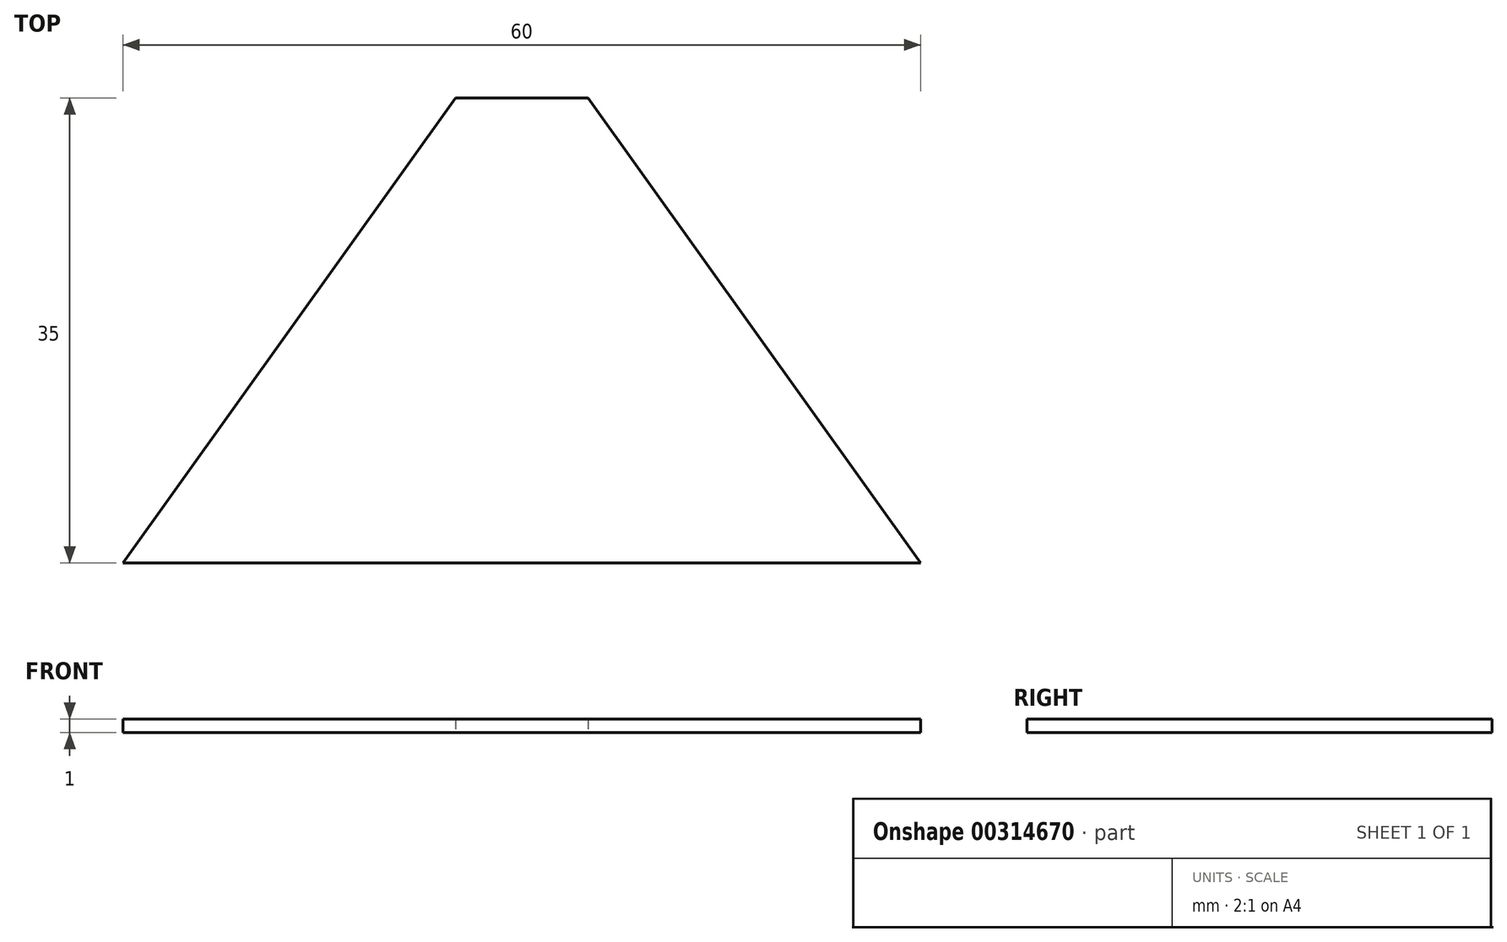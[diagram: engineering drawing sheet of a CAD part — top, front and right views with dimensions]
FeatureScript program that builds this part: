
annotation { "Feature Type Name" : "Feature", "Feature Type Description" : "" }
export const myFeature = defineFeature(function(context is Context, id is Id, definition is map)
    precondition{}
    {
        {
            var Q0;
            Q0=qCreatedBy(makeId("Top.planeOp"),FACE);
            var sketch = newSketch(context, id + "F0", { "sketchPlane" : qUnion([Q0])});
            skLineSegment(sketch, "E0", {"start": v(0, 0) * mm, "end": v(0, 35) * mm, "construction": true});
            skLineSegment(sketch, "E1", {"start": v(0, 0) * mm, "end": v(-30, 0) * mm});
            skLineSegment(sketch, "E2", {"start": v(0, 35) * mm, "end": v(-5, 35) * mm});
            skLineSegment(sketch, "E3", {"start": v(-5, 35) * mm, "end": v(-30, 0) * mm});
            skLineSegment(sketch, "E4.MirrorCS", {"start": v(0, 35) * mm, "end": v(5, 35) * mm});
            skLineSegment(sketch, "E5.MirrorCS", {"start": v(5, 35) * mm, "end": v(30, 0) * mm});
            skLineSegment(sketch, "E6.MirrorCS", {"start": v(0, 0) * mm, "end": v(30, 0) * mm});
            skSolve(sketch);
        }
        {
            var Q0;
            Q0=makeQuery(id+"F0.imprint","IMPRINT",FACE,{"disambiguationData":[TD([[makeQuery(id+"F0.imprint","IMPRINT",EDGE,{"derivedFrom":sQuery(id+"F0.wireOp",EDGE,"E1")}),-1.0]])]});
            extrude(context, id + "F1", {"entities" : qUnion([Q0]), "depth" : 1 * mm});
        }
    });
